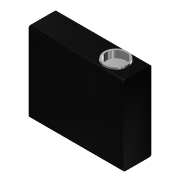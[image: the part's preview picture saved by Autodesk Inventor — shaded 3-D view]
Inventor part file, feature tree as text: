
AUTODESK INVENTOR PART (.ipt)
format: ipt  version: 2014 (Build 180170000, 170)  size: 123,904 bytes
history: native  units: mm
features: extrude x3, sketch x3, fillet x2
ambient origin geometry x8: Origin, YZ Plane, XZ Plane, XY Plane, X Axis, Y Axis, Z Axis, Center Point
bodies: Solid1 (feature_tree)
feature tree (8):
  extrude  "Extrusion1"  Depth=220.98mm
  extrude  "Extrusion2"  Depth=78.74mm
  extrude  "Extrusion3"  Depth=78.74mm
  fillet  "Fillet1"  Radius=39.37mm
  fillet  "Fillet2"  Radius=5.0mm
  sketch  "Sketch1"  dims[d0=264.16mm d1=220.98mm]
  sketch  "Sketch2"  dims[d2=78.74mm d3=0.0mm d4=60.0mm]
  sketch  "Sketch3"  dims[d5=65.0mm d6=78.74mm d7=39.37mm d8=5.0mm d9=0.0mm d10=55.0mm d11=20.0mm d12=0.0mm d13=6.0mm d14=1.0mm]
